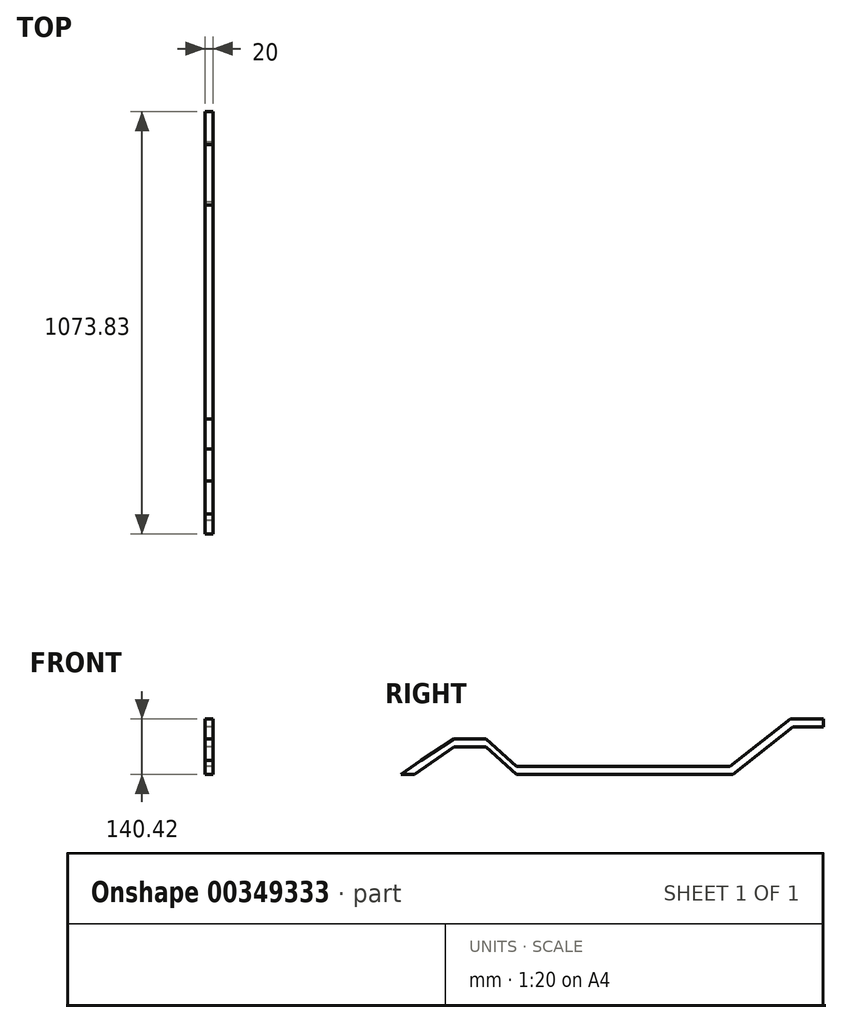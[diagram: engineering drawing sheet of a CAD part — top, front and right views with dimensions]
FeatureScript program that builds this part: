
annotation { "Feature Type Name" : "Feature", "Feature Type Description" : "" }
export const myFeature = defineFeature(function(context is Context, id is Id, definition is map)
    precondition{}
    {
        {
            var Q0;
            Q0=qCreatedBy(makeId("Right.planeOp"),FACE);
            var sketch = newSketch(context, id + "F0", { "sketchPlane" : qUnion([Q0])});
            skLineSegment(sketch, "E0.bottom", {"start": v(-275, 9.44) * mm, "end": v(275, 9.44) * mm});
            skLineSegment(sketch, "E0.top", {"start": v(-275, -10.56) * mm, "end": v(275, -10.56) * mm});
            skLineSegment(sketch, "E0.left", {"start": v(-275, 9.44) * mm, "end": v(-275, -10.56) * mm});
            skLineSegment(sketch, "E0.right", {"start": v(275, 9.44) * mm, "end": v(275, -10.56) * mm});
            skPoint(sketch, "E0.middle", {"position": v(0, -0.56) * mm});
            skLineSegment(sketch, "E1", {"start": v(275, -10.56) * mm, "end": v(453.85, 129.86) * mm});
            skLineSegment(sketch, "E2", {"start": v(453.85, 129.86) * mm, "end": v(405.55, 129.86) * mm});
            skLineSegment(sketch, "E3", {"start": v(301.24, 10.04) * mm, "end": v(288.9, 25.77) * mm});
            skLineSegment(sketch, "E4", {"start": v(288.9, 25.77) * mm, "end": v(268.09, 9.44) * mm});
            skLineSegment(sketch, "E5", {"start": v(268.09, 9.44) * mm, "end": v(421.47, 129.86) * mm});
            skLineSegment(sketch, "E6", {"start": v(421.47, 129.86) * mm, "end": v(505.59, 129.86) * mm});
            skLineSegment(sketch, "E7", {"start": v(505.59, 129.86) * mm, "end": v(505.59, 109.75) * mm});
            skLineSegment(sketch, "E8", {"start": v(505.59, 109.75) * mm, "end": v(428.24, 109.75) * mm});
            skLineSegment(sketch, "E9", {"start": v(332.04, 59.65) * mm, "end": v(-413.02, 59.65) * mm});
            skPoint(sketch, "E9.startSnap0", {"position": v(364.43, 59.65) * mm});
            skLineSegment(sketch, "E10", {"start": v(-275, 9.44) * mm, "end": v(-330.04, 59.65) * mm});
            skLineSegment(sketch, "E11", {"start": v(-330.04, 59.65) * mm, "end": v(-432.78, 59.65) * mm});
            skLineSegment(sketch, "E12", {"start": v(-432.78, 59.65) * mm, "end": v(-432.78, 79.65) * mm});
            skLineSegment(sketch, "E13", {"start": v(-432.78, 79.65) * mm, "end": v(-271.87, 79.65) * mm});
            skLineSegment(sketch, "E14", {"start": v(-302.52, 34.54) * mm, "end": v(-289.04, 49.32) * mm});
            skLineSegment(sketch, "E15", {"start": v(-275, -10.56) * mm, "end": v(-373.9, 79.65) * mm});
            skLineSegment(sketch, "E16", {"start": v(-330.04, 59.65) * mm, "end": v(-351.97, 79.65) * mm});
            skLineSegment(sketch, "E17", {"start": v(-432.78, 59.65) * mm, "end": v(-533.31, -10.56) * mm});
            skLineSegment(sketch, "E18", {"start": v(-505.93, 8.56) * mm, "end": v(-517.38, 24.95) * mm});
            skLineSegment(sketch, "E19", {"start": v(-432.78, 79.65) * mm, "end": v(-517.38, 24.95) * mm});
            skLineSegment(sketch, "E20", {"start": v(-517.38, 24.95) * mm, "end": v(-568.24, -10.56) * mm});
            skLineSegment(sketch, "E21", {"start": v(-568.24, -10.56) * mm, "end": v(-533.31, -10.56) * mm});
            skSolve(sketch);
        }
        {
            var Q0;
            {var subQ0=sQuery(id+"F0.wireOp",EDGE,"E12");Q0=makeQuery(id+"F0.imprint","IMPRINT",FACE,{"disambiguationData":[TD([[makeQuery(id+"F0.imprint","IMPRINT",EDGE,{"derivedFrom":subQ0}),-1.0]])]});}
            var Q1;
            {var subQ0=sQuery(id+"F0.wireOp",EDGE,"E16");Q1=makeQuery(id+"F0.imprint","IMPRINT",FACE,{"disambiguationData":[TD([[makeQuery(id+"F0.imprint","IMPRINT",EDGE,{"derivedFrom":subQ0}),1.0]])]});}
            var Q2;
            {var subQ5=sQuery(id+"F0.wireOp",EDGE,"E0.left");Q2=makeQuery(id+"F0.imprint","IMPRINT",FACE,{"disambiguationData":[TD([[makeQuery(id+"F0.imprint","IMPRINT",EDGE,{"derivedFrom":subQ5}),-1.0]])]});}
            var Q3;
            Q3=makeQuery(id+"F0.imprint","IMPRINT",FACE,{"disambiguationData":[TD([[makeQuery(id+"F0.imprint","IMPRINT",EDGE,{"derivedFrom":sQuery(id+"F0.wireOp",EDGE,"E0.top")}),1.0]])]});
            var Q4;
            {var subQ1=sQuery(id+"F0.wireOp",EDGE,"E3");Q4=makeQuery(id+"F0.imprint","IMPRINT",FACE,{"disambiguationData":[TD([[makeQuery(id+"F0.imprint","IMPRINT",EDGE,{"derivedFrom":subQ1}),-1.0]])]});}
            var Q5;
            {var subQ4=sQuery(id+"F0.wireOp",EDGE,"E7");Q5=makeQuery(id+"F0.imprint","IMPRINT",FACE,{"disambiguationData":[TD([[makeQuery(id+"F0.imprint","IMPRINT",EDGE,{"derivedFrom":subQ4}),-1.0]])]});}
            var Q6;
            {var subQ2=sQuery(id+"F0.wireOp",EDGE,"E0.right");Q6=makeQuery(id+"F0.imprint","IMPRINT",FACE,{"disambiguationData":[TD([[makeQuery(id+"F0.imprint","IMPRINT",EDGE,{"derivedFrom":subQ2}),1.0]])]});}
            var Q7;
            {var subQ0=sQuery(id+"F0.wireOp",EDGE,"E12");Q7=makeQuery(id+"F0.imprint","IMPRINT",FACE,{"disambiguationData":[TD([[makeQuery(id+"F0.imprint","IMPRINT",EDGE,{"derivedFrom":subQ0}),1.0]])]});}
            var Q8;
            {var subQ2=sQuery(id+"F0.wireOp",EDGE,"E18");Q8=makeQuery(id+"F0.imprint","IMPRINT",FACE,{"disambiguationData":[TD([[makeQuery(id+"F0.imprint","IMPRINT",EDGE,{"derivedFrom":subQ2}),1.0]])]});}
            extrude(context, id + "F1", {"entities" : qUnion([Q0, Q1, Q2, Q3, Q4, Q5, Q6, Q7, Q8]), "depth" : 20 * mm});
        }
    });
